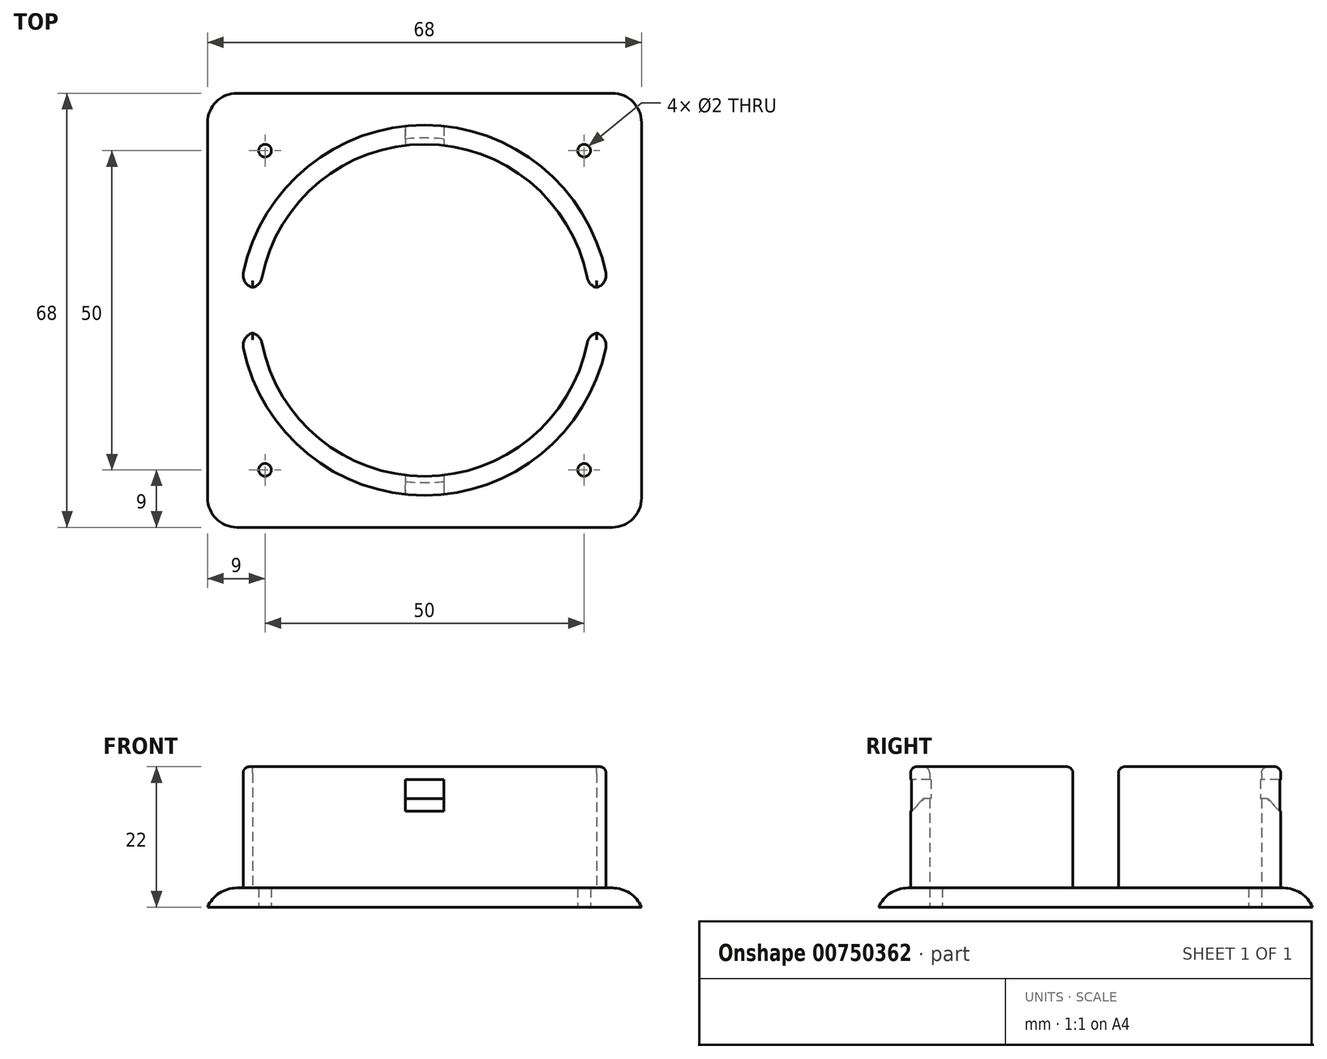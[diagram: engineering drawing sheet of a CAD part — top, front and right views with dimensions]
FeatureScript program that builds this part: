
annotation { "Feature Type Name" : "Feature", "Feature Type Description" : "" }
export const myFeature = defineFeature(function(context is Context, id is Id, definition is map)
    precondition{}
    {
        {
            var Q0;
            Q0=qCreatedBy(makeId("Top.planeOp"),FACE);
            var sketch = newSketch(context, id + "F0", { "sketchPlane" : qUnion([Q0])});
            skArc(sketch, "E0", {"start": v(25.76, 3.5) * mm, "mid": v(0, 26) * mm, "end": v(-25.76, 3.5) * mm});
            skArc(sketch, "E1.0", {"start": v(28.79, 3.5) * mm, "mid": v(0, 29) * mm, "end": v(-28.79, 3.5) * mm});
            skLineSegment(sketch, "E2.bottom", {"start": v(-34, 34) * mm, "end": v(34, 34) * mm});
            skLineSegment(sketch, "E2.top", {"start": v(-34, -34) * mm, "end": v(34, -34) * mm});
            skLineSegment(sketch, "E2.left", {"start": v(-34, 34) * mm, "end": v(-34, -34) * mm});
            skLineSegment(sketch, "E2.right", {"start": v(34, 34) * mm, "end": v(34, -34) * mm});
            skLineSegment(sketch, "E3.bottom", {"start": v(-29, 29) * mm, "end": v(29, 29) * mm, "construction": true});
            skLineSegment(sketch, "E3.top", {"start": v(-29, -29) * mm, "end": v(29, -29) * mm, "construction": true});
            skLineSegment(sketch, "E3.left", {"start": v(-29, 29) * mm, "end": v(-29, -29) * mm, "construction": true});
            skLineSegment(sketch, "E3.right", {"start": v(29, 29) * mm, "end": v(29, -29) * mm, "construction": true});
            skCircle(sketch, "E4", {"center": v(-25, 25) * mm, "radius": 1 * mm});
            skLineSegment(sketch, "E5", {"start": v(-29, 29) * mm, "end": v(-34, 34) * mm, "construction": true});
            skLineSegment(sketch, "E6", {"start": v(-34, -34) * mm, "end": v(-29, -29) * mm, "construction": true});
            skLineSegment(sketch, "E7", {"start": v(29, -29) * mm, "end": v(34, -34) * mm, "construction": true});
            skLineSegment(sketch, "E8", {"start": v(29, 29) * mm, "end": v(34, 34) * mm, "construction": true});
            skLineSegment(sketch, "E9.bottom", {"start": v(-26, 26) * mm, "end": v(-24, 26) * mm, "construction": true});
            skLineSegment(sketch, "E9.top", {"start": v(-26, 24) * mm, "end": v(-24, 24) * mm, "construction": true});
            skLineSegment(sketch, "E9.left", {"start": v(-26, 26) * mm, "end": v(-26, 24) * mm, "construction": true});
            skLineSegment(sketch, "E9.right", {"start": v(-24, 26) * mm, "end": v(-24, 24) * mm, "construction": true});
            skCircle(sketch, "E10", {"center": v(25, 25) * mm, "radius": 1 * mm});
            skLineSegment(sketch, "E11.bottom", {"start": v(24, 26) * mm, "end": v(26, 26) * mm, "construction": true});
            skLineSegment(sketch, "E11.top", {"start": v(24, 24) * mm, "end": v(26, 24) * mm, "construction": true});
            skLineSegment(sketch, "E11.left", {"start": v(24, 26) * mm, "end": v(24, 24) * mm, "construction": true});
            skLineSegment(sketch, "E11.right", {"start": v(26, 26) * mm, "end": v(26, 24) * mm, "construction": true});
            skCircle(sketch, "E12", {"center": v(25, -25) * mm, "radius": 1 * mm});
            skLineSegment(sketch, "E13.bottom", {"start": v(24, -24) * mm, "end": v(26, -24) * mm, "construction": true});
            skLineSegment(sketch, "E13.top", {"start": v(24, -26) * mm, "end": v(26, -26) * mm, "construction": true});
            skLineSegment(sketch, "E13.left", {"start": v(24, -24) * mm, "end": v(24, -26) * mm, "construction": true});
            skLineSegment(sketch, "E13.right", {"start": v(26, -24) * mm, "end": v(26, -26) * mm, "construction": true});
            skCircle(sketch, "E14", {"center": v(-25, -25) * mm, "radius": 1 * mm});
            skLineSegment(sketch, "E15.bottom", {"start": v(-26, -24) * mm, "end": v(-24, -24) * mm, "construction": true});
            skLineSegment(sketch, "E15.top", {"start": v(-26, -26) * mm, "end": v(-24, -26) * mm, "construction": true});
            skLineSegment(sketch, "E15.left", {"start": v(-26, -24) * mm, "end": v(-26, -26) * mm, "construction": true});
            skLineSegment(sketch, "E15.right", {"start": v(-24, -24) * mm, "end": v(-24, -26) * mm, "construction": true});
            skLineSegment(sketch, "E16", {"start": v(0, 0) * mm, "end": v(45.2, 0) * mm, "construction": true});
            skPoint(sketch, "E16.endSnap0", {"position": v(34, 0) * mm});
            skLineSegment(sketch, "E17", {"start": v(0, 0) * mm, "end": v(-38.32, 0) * mm, "construction": true});
            skLineSegment(sketch, "E18", {"start": v(25.76, 3.5) * mm, "end": v(28.79, 3.5) * mm});
            skLineSegment(sketch, "E19", {"start": v(25.76, -3.5) * mm, "end": v(28.79, -3.5) * mm});
            skLineSegment(sketch, "E20", {"start": v(0, 3.5) * mm, "end": v(0, -3.5) * mm, "construction": true});
            skPoint(sketch, "E21.orphan", {"position": v(0, 3.5) * mm});
            skPoint(sketch, "E22.orphan", {"position": v(0, -3.5) * mm});
            skLineSegment(sketch, "E23", {"start": v(-25.76, 3.5) * mm, "end": v(-28.79, 3.5) * mm});
            skLineSegment(sketch, "E24", {"start": v(-25.76, -3.5) * mm, "end": v(-28.79, -3.5) * mm});
            skPoint(sketch, "E25.orphan", {"position": v(-1.44, 3.5) * mm});
            skArc(sketch, "E26.trimOffspring", {"start": v(-25.76, -3.5) * mm, "mid": v(0, -26) * mm, "end": v(25.76, -3.5) * mm});
            skArc(sketch, "E27.trimOffspring", {"start": v(-28.79, -3.5) * mm, "mid": v(0, -29) * mm, "end": v(28.79, -3.5) * mm});
            skSolve(sketch);
        }
        {
            var Q0;
            Q0=makeQuery(id+"F0.imprint","IMPRINT",FACE,{"disambiguationData":[TD([[makeQuery(id+"F0.imprint","IMPRINT",EDGE,{"derivedFrom":sQuery(id+"F0.wireOp",EDGE,"E0")}),1.0]])]});
            extrude(context, id + "F1", {"entities" : qUnion([Q0]), "depth" : 3 * mm, "offsetDistance" : 25 * mm});
        }
        {
            var Q0;
            Q0=makeQuery(id+"F1.opExtrude","CAP_EDGE",EDGE,{"disambiguationData":[OSD([sQuery(id+"F0.wireOp",EDGE,"E2.top")])],"isStart":false});
            var Q1;
            Q1=makeQuery(id+"F1.opExtrude","CAP_EDGE",EDGE,{"disambiguationData":[OSD([sQuery(id+"F0.wireOp",EDGE,"E2.left")])],"isStart":false});
            var Q2;
            Q2=makeQuery(id+"F1.opExtrude","CAP_EDGE",EDGE,{"disambiguationData":[OSD([sQuery(id+"F0.wireOp",EDGE,"E2.right")])],"isStart":false});
            var Q3;
            Q3=makeQuery(id+"F1.opExtrude","CAP_EDGE",EDGE,{"disambiguationData":[OSD([sQuery(id+"F0.wireOp",EDGE,"E2.bottom")])],"isStart":false});
            fillet(context, id + "F2", {"entities" : qUnion([Q0, Q1, Q2, Q3]), "radius" : 5 * mm, "tangentPropagation" : true, "allowEdgeOverflow" : false});
        }
        {
            var Q0;
            Q0=makeQuery(id+"F0.imprint","IMPRINT",FACE,{"disambiguationData":[TD([[makeQuery(id+"F0.imprint","IMPRINT",EDGE,{"derivedFrom":sQuery(id+"F0.wireOp",EDGE,"E0")}),-1.0]])]});
            var Q1;
            Q1=makeQuery(id+"F0.imprint","IMPRINT",FACE,{"disambiguationData":[TD([[makeQuery(id+"F0.imprint","IMPRINT",EDGE,{"derivedFrom":sQuery(id+"F0.wireOp",EDGE,"E19")}),-1.0]])]});
            extrude(context, id + "F3", {"entities" : qUnion([Q0, Q1]), "operationType" : NewBodyOperationType.ADD, "depth" : 22 * mm, "offsetDistance" : 25 * mm});
        }
        {
            var Q0;
            Q0=makeQuery(id+"F3.opExtrude","SWEPT_EDGE",EDGE,{"disambiguationData":[OSD([sQuery(id+"F0.wireOp",EDGE,"E1.0"),sQuery(id+"F0.wireOp",EDGE,"E23")])]});
            var Q1;
            Q1=makeQuery(id+"F3.opExtrude","SWEPT_EDGE",EDGE,{"disambiguationData":[OSD([sQuery(id+"F0.wireOp",EDGE,"E0"),sQuery(id+"F0.wireOp",EDGE,"E23")])]});
            var Q2;
            Q2=makeQuery(id+"F3.opExtrude","SWEPT_EDGE",EDGE,{"disambiguationData":[OSD([sQuery(id+"F0.wireOp",EDGE,"E24"),sQuery(id+"F0.wireOp",EDGE,"E27.trimOffspring")])]});
            var Q3;
            Q3=makeQuery(id+"F3.opExtrude","SWEPT_EDGE",EDGE,{"disambiguationData":[OSD([sQuery(id+"F0.wireOp",EDGE,"E24"),sQuery(id+"F0.wireOp",EDGE,"E26.trimOffspring")])]});
            var Q4;
            Q4=makeQuery(id+"F3.opExtrude","SWEPT_EDGE",EDGE,{"disambiguationData":[OSD([sQuery(id+"F0.wireOp",EDGE,"E1.0"),sQuery(id+"F0.wireOp",EDGE,"E18")])]});
            var Q5;
            Q5=makeQuery(id+"F3.opExtrude","SWEPT_EDGE",EDGE,{"disambiguationData":[OSD([sQuery(id+"F0.wireOp",EDGE,"E0"),sQuery(id+"F0.wireOp",EDGE,"E18")])]});
            var Q6;
            Q6=makeQuery(id+"F3.opExtrude","SWEPT_EDGE",EDGE,{"disambiguationData":[OSD([sQuery(id+"F0.wireOp",EDGE,"E19"),sQuery(id+"F0.wireOp",EDGE,"E27.trimOffspring")])]});
            var Q7;
            Q7=makeQuery(id+"F3.opExtrude","SWEPT_EDGE",EDGE,{"disambiguationData":[OSD([sQuery(id+"F0.wireOp",EDGE,"E19"),sQuery(id+"F0.wireOp",EDGE,"E26.trimOffspring")])]});
            fillet(context, id + "F4", {"entities" : qUnion([Q0, Q1, Q2, Q3, Q4, Q5, Q6, Q7]), "radius" : 2 * mm, "tangentPropagation" : true, "allowEdgeOverflow" : false});
        }
        {
            var Q0;
            Q0=makeQuery(id+"F3.opExtrude","CAP_EDGE",EDGE,{"disambiguationData":[OSD([sQuery(id+"F0.wireOp",EDGE,"E0")])],"isStart":false});
            var Q1;
            Q1=makeQuery(id+"F3.opExtrude","CAP_EDGE",EDGE,{"disambiguationData":[OSD([sQuery(id+"F0.wireOp",EDGE,"E1.0")])],"isStart":false});
            var Q2;
            {var subQ0=sQuery(id+"F0.wireOp",EDGE,"E18");var subQ1=sQuery(id+"F0.wireOp",EDGE,"E1.0");Q2=makeQuery(id+"F4.opFillet","BLEND_EDGE",EDGE,{"blendedFrom":[makeQuery(id+"F3.opExtrude","SWEPT_EDGE",EDGE,{"disambiguationData":[OSD([subQ1,subQ0])]}),makeQuery(id+"F3.opExtrude","CAP_FACE",FACE,{"disambiguationData":[OSD([sQuery(id+"F0.wireOp",EDGE,"E0"),subQ1,subQ0,sQuery(id+"F0.wireOp",EDGE,"E23")])],"isStart":false})],"blendedInto":[makeQuery(id+"F3.opExtrude","CAP_FACE",FACE,{"disambiguationData":[OSD([sQuery(id+"F0.wireOp",EDGE,"E0"),subQ1,subQ0,sQuery(id+"F0.wireOp",EDGE,"E23")])],"isStart":false})]});}
            var Q3;
            Q3=makeQuery(id+"F3.opExtrude","CAP_EDGE",EDGE,{"disambiguationData":[OSD([sQuery(id+"F0.wireOp",EDGE,"E27.trimOffspring")])],"isStart":false});
            var Q4;
            Q4=makeQuery(id+"F3.opExtrude","CAP_EDGE",EDGE,{"disambiguationData":[OSD([sQuery(id+"F0.wireOp",EDGE,"E26.trimOffspring")])],"isStart":false});
            fillet(context, id + "F5", {"entities" : qUnion([Q0, Q1, Q2, Q3, Q4]), "radius" : 1 * mm, "tangentPropagation" : true, "allowEdgeOverflow" : false});
        }
        {
            var Q0;
            Q0=qCreatedBy(makeId("Front.planeOp"),FACE);
            var sketch = newSketch(context, id + "F6", { "sketchPlane" : qUnion([Q0])});
            skLineSegment(sketch, "E28.bottom", {"start": v(3, 20) * mm, "end": v(-3, 20) * mm});
            skLineSegment(sketch, "E28.top", {"start": v(3, 17) * mm, "end": v(-3, 17) * mm});
            skLineSegment(sketch, "E28.left", {"start": v(3, 20) * mm, "end": v(3, 17) * mm});
            skLineSegment(sketch, "E28.right", {"start": v(-3, 20) * mm, "end": v(-3, 17) * mm});
            skLineSegment(sketch, "E29", {"start": v(0, 31) * mm, "end": v(0, -9) * mm, "construction": true});
            skLineSegment(sketch, "E30", {"start": v(3, 20) * mm, "end": v(-3, 17) * mm, "construction": true});
            skLineSegment(sketch, "E31", {"start": v(-3, 20) * mm, "end": v(3, 17) * mm, "construction": true});
            skSolve(sketch);
        }
        {
            var Q0;
            Q0 = qSketchRegion(id + "F6", true);
            extrude(context, id + "F7", {"entities" : qUnion([Q0]), "operationType" : NewBodyOperationType.REMOVE, "endBound" : BoundingType.SYMMETRIC, "oppositeDirection" : true, "depth" : 70 * mm, "offsetDistance" : 25 * mm});
        }
        {
            var Q0;
            Q0=makeQuery(id+"F7.boolean.opBoolean","INTERSECT",EDGE,{"derivedFrom":[makeQuery(id+"F3.opExtrude","SWEPT_FACE",FACE,{"disambiguationData":[OSD([sQuery(id+"F0.wireOp",EDGE,"E1.0")])]}),makeQuery(id+"F7.opExtrude","SWEPT_FACE",FACE,{"disambiguationData":[OSD([sQuery(id+"F6.wireOp",EDGE,"E28.top")])]})]});
            var Q1;
            Q1=makeQuery(id+"F7.boolean.opBoolean","INTERSECT",EDGE,{"derivedFrom":[makeQuery(id+"F3.opExtrude","SWEPT_FACE",FACE,{"disambiguationData":[OSD([sQuery(id+"F0.wireOp",EDGE,"E27.trimOffspring")])]}),makeQuery(id+"F7.opExtrude","SWEPT_FACE",FACE,{"disambiguationData":[OSD([sQuery(id+"F6.wireOp",EDGE,"E28.top")])]})]});
            chamfer(context, id + "F8", {"entities" : qUnion([Q0, Q1]), "width" : 2 * mm, "tangentPropagation" : true});
        }
        {
            var Q0;
            Q0=makeQuery(id+"F2.opFillet","BLEND_EDGE",EDGE,{"blendedFrom":[makeQuery(id+"F1.opExtrude","CAP_EDGE",EDGE,{"disambiguationData":[OSD([sQuery(id+"F0.wireOp",EDGE,"E2.bottom")])],"isStart":false}),makeQuery(id+"F1.opExtrude","CAP_EDGE",EDGE,{"disambiguationData":[OSD([sQuery(id+"F0.wireOp",EDGE,"E2.left")])],"isStart":false})],"blendedInto":[]});
            var Q1;
            Q1=makeQuery(id+"F2.opFillet","BLEND_EDGE",EDGE,{"blendedFrom":[makeQuery(id+"F1.opExtrude","CAP_EDGE",EDGE,{"disambiguationData":[OSD([sQuery(id+"F0.wireOp",EDGE,"E2.top")])],"isStart":false}),makeQuery(id+"F1.opExtrude","CAP_EDGE",EDGE,{"disambiguationData":[OSD([sQuery(id+"F0.wireOp",EDGE,"E2.left")])],"isStart":false})],"blendedInto":[]});
            var Q2;
            Q2=makeQuery(id+"F2.opFillet","BLEND_EDGE",EDGE,{"blendedFrom":[makeQuery(id+"F1.opExtrude","CAP_EDGE",EDGE,{"disambiguationData":[OSD([sQuery(id+"F0.wireOp",EDGE,"E2.top")])],"isStart":false}),makeQuery(id+"F1.opExtrude","CAP_EDGE",EDGE,{"disambiguationData":[OSD([sQuery(id+"F0.wireOp",EDGE,"E2.right")])],"isStart":false})],"blendedInto":[]});
            var Q3;
            Q3=makeQuery(id+"F2.opFillet","BLEND_EDGE",EDGE,{"blendedFrom":[makeQuery(id+"F1.opExtrude","CAP_EDGE",EDGE,{"disambiguationData":[OSD([sQuery(id+"F0.wireOp",EDGE,"E2.bottom")])],"isStart":false}),makeQuery(id+"F1.opExtrude","CAP_EDGE",EDGE,{"disambiguationData":[OSD([sQuery(id+"F0.wireOp",EDGE,"E2.right")])],"isStart":false})],"blendedInto":[]});
            fillet(context, id + "F9", {"entities" : qUnion([Q0, Q1, Q2, Q3]), "radius" : 5 * mm, "tangentPropagation" : true, "allowEdgeOverflow" : false});
        }
    });
